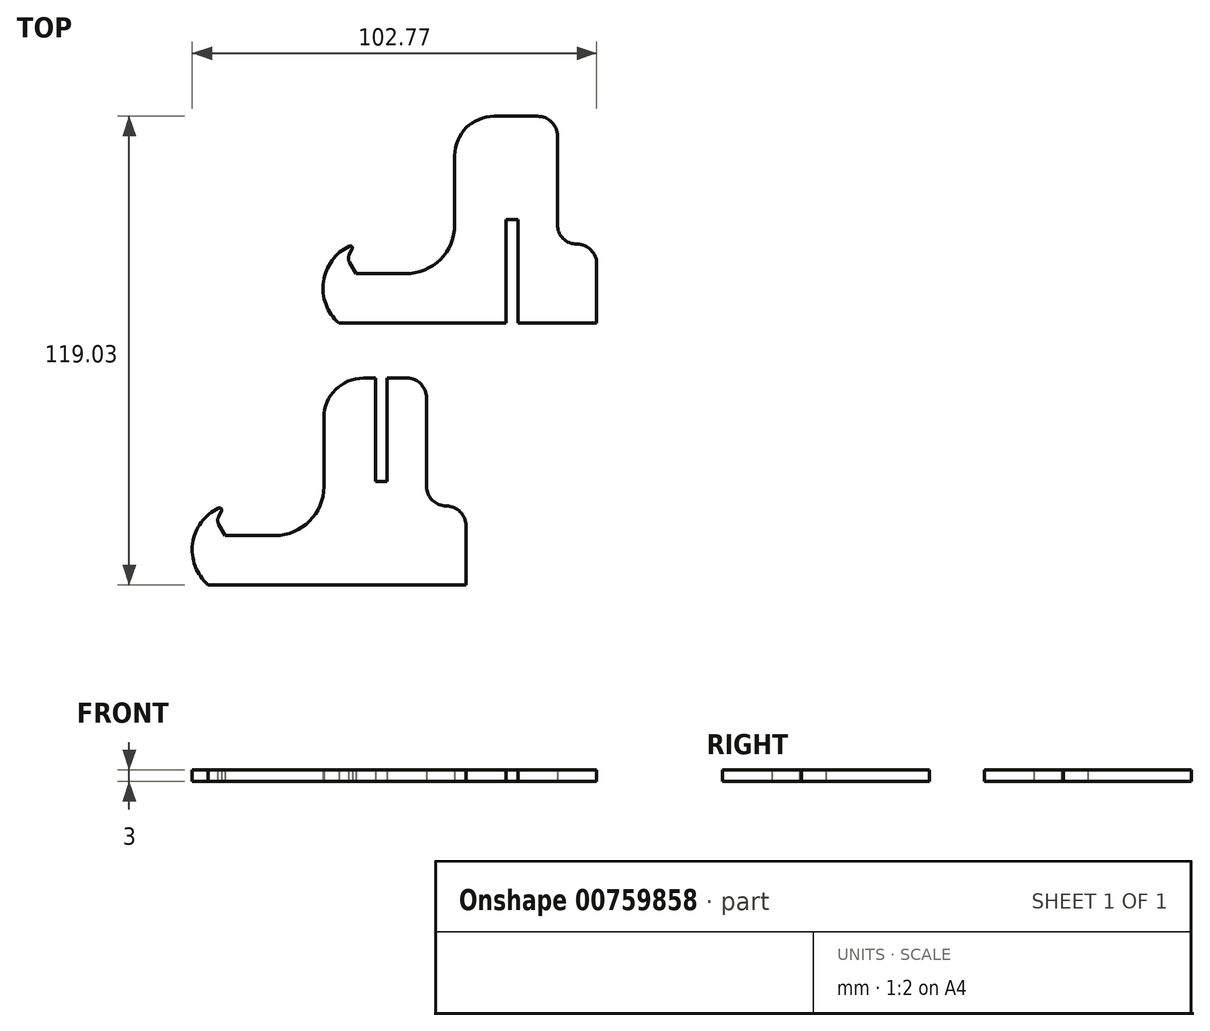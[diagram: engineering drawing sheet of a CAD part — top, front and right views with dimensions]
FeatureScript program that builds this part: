
annotation { "Feature Type Name" : "Feature", "Feature Type Description" : "" }
export const myFeature = defineFeature(function(context is Context, id is Id, definition is map)
    precondition{}
    {
        {
            var Q0;
            Q0=qCreatedBy(makeId("Top.planeOp"),FACE);
            var sketch = newSketch(context, id + "F0", { "sketchPlane" : qUnion([Q0])});
            skLineSegment(sketch, "E0", {"start": v(-16.1, 20.7) * mm, "end": v(-28.7, 20.7) * mm});
            skLineSegment(sketch, "E1", {"start": v(-28.7, 20.7) * mm, "end": v(-30.35, 23.55) * mm});
            skPoint(sketch, "E2.visualSharp", {"position": v(3.9, 50.7) * mm});
            skPoint(sketch, "E3.visualSharp", {"position": v(3.9, 20.7) * mm});
            skArc(sketch, "E3.filletArc", {"start": v(-16.1, 20.7) * mm, "mid": v(-7.26, 24.35) * mm, "end": v(-3.6, 33.2) * mm});
            skPoint(sketch, "E4.second.point", {"position": v(-37.03, 18.2) * mm});
            skPoint(sketch, "E5.orphan", {"position": v(-37.03, 28.2) * mm});
            skPoint(sketch, "E6.0.end.orphan", {"position": v(-37.03, 8.2) * mm});
            skLineSegment(sketch, "E7", {"start": v(-30.43, 25.38) * mm, "end": v(-29.67, 27.05) * mm});
            skArc(sketch, "E8", {"start": v(-30.34, 27.7) * mm, "mid": v(-36.97, 18.68) * mm, "end": v(-33.03, 8.2) * mm});
            skPoint(sketch, "E9.orphan", {"position": v(-33.03, 28.2) * mm});
            skPoint(sketch, "E10.visualSharp", {"position": v(-30.86, 24.44) * mm});
            skArc(sketch, "E10.filletArc", {"start": v(-30.43, 25.38) * mm, "mid": v(-30.61, 24.45) * mm, "end": v(-30.35, 23.55) * mm});
            skPoint(sketch, "E11.visualSharp", {"position": v(-29.14, 28.2) * mm});
            skArc(sketch, "E11.filletArc", {"start": v(-29.67, 27.05) * mm, "mid": v(-29.77, 27.61) * mm, "end": v(-30.34, 27.7) * mm});
            skLineSegment(sketch, "E12", {"start": v(-3.6, 33.2) * mm, "end": v(-3.6, 50.7) * mm});
            skPoint(sketch, "E13.visualSharp", {"position": v(-3.6, 60.7) * mm});
            skArc(sketch, "E13.filletArc", {"start": v(6.4, 60.7) * mm, "mid": v(-0.67, 57.76) * mm, "end": v(-3.6, 50.7) * mm});
            skLineSegment(sketch, "E14", {"start": v(-33.03, 8.2) * mm, "end": v(9.47, 8.2) * mm});
            skLineSegment(sketch, "E15", {"start": v(9.47, 8.2) * mm, "end": v(9.47, 34.44) * mm});
            skLineSegment(sketch, "E16", {"start": v(9.47, 34.44) * mm, "end": v(12.47, 34.44) * mm});
            skLineSegment(sketch, "E17", {"start": v(12.47, 34.44) * mm, "end": v(12.47, 8.2) * mm});
            skLineSegment(sketch, "E18", {"start": v(12.47, 8.2) * mm, "end": v(32.47, 8.2) * mm});
            skLineSegment(sketch, "E19", {"start": v(32.47, 8.2) * mm, "end": v(32.47, 23.2) * mm});
            skLineSegment(sketch, "E20", {"start": v(17.47, 60.7) * mm, "end": v(6.4, 60.7) * mm});
            skPoint(sketch, "E21.visualSharp", {"position": v(32.47, 60.7) * mm});
            skLineSegment(sketch, "E22", {"start": v(22.47, 33.2) * mm, "end": v(22.47, 55.7) * mm});
            skLineSegment(sketch, "E23", {"start": v(17.47, 60.7) * mm, "end": v(17.47, 60.7) * mm});
            skLineSegment(sketch, "E24.0", {"start": v(27.47, 28.2) * mm, "end": v(27.47, 28.2) * mm});
            skPoint(sketch, "E25.orphan", {"position": v(22.47, 8.2) * mm});
            skPoint(sketch, "E26.visualSharp", {"position": v(22.47, 60.7) * mm});
            skArc(sketch, "E26.filletArc", {"start": v(22.47, 55.7) * mm, "mid": v(21, 59.23) * mm, "end": v(17.47, 60.7) * mm});
            skPoint(sketch, "E27.visualSharp", {"position": v(22.47, 28.2) * mm});
            skArc(sketch, "E27.filletArc", {"start": v(22.47, 33.2) * mm, "mid": v(23.94, 29.66) * mm, "end": v(27.47, 28.2) * mm});
            skPoint(sketch, "E28.visualSharp", {"position": v(32.47, 28.2) * mm});
            skArc(sketch, "E28.filletArc", {"start": v(32.47, 23.2) * mm, "mid": v(31, 26.73) * mm, "end": v(27.47, 28.2) * mm});
            skLineSegment(sketch, "E29", {"start": v(-18.7, 20.7) * mm, "end": v(0.7, 62.1) * mm, "construction": true});
            skLineSegment(sketch, "E30", {"start": v(-49.32, -45.84) * mm, "end": v(-61.91, -45.84) * mm});
            skLineSegment(sketch, "E31", {"start": v(-61.91, -45.84) * mm, "end": v(-63.56, -42.99) * mm});
            skPoint(sketch, "E32.visualSharp", {"position": v(-29.32, -15.84) * mm});
            skPoint(sketch, "E33.visualSharp", {"position": v(-29.32, -45.84) * mm});
            skArc(sketch, "E33.filletArc", {"start": v(-49.32, -45.84) * mm, "mid": v(-40.48, -42.18) * mm, "end": v(-36.82, -33.34) * mm});
            skPoint(sketch, "E34.second.point", {"position": v(-70.24, -48.34) * mm});
            skPoint(sketch, "E35.orphan", {"position": v(-70.24, -38.34) * mm});
            skPoint(sketch, "E36.0.end.orphan", {"position": v(-70.24, -58.34) * mm});
            skLineSegment(sketch, "E37", {"start": v(-63.65, -41.15) * mm, "end": v(-62.88, -39.49) * mm});
            skArc(sketch, "E38", {"start": v(-63.55, -38.82) * mm, "mid": v(-70.19, -47.85) * mm, "end": v(-66.24, -58.34) * mm});
            skPoint(sketch, "E39.orphan", {"position": v(-66.24, -38.34) * mm});
            skPoint(sketch, "E40.visualSharp", {"position": v(-64.08, -42.1) * mm});
            skArc(sketch, "E40.filletArc", {"start": v(-63.65, -41.15) * mm, "mid": v(-63.83, -42.08) * mm, "end": v(-63.56, -42.99) * mm});
            skPoint(sketch, "E41.visualSharp", {"position": v(-62.36, -38.34) * mm});
            skArc(sketch, "E41.filletArc", {"start": v(-62.88, -39.49) * mm, "mid": v(-62.99, -38.92) * mm, "end": v(-63.55, -38.82) * mm});
            skLineSegment(sketch, "E42", {"start": v(-36.82, -33.34) * mm, "end": v(-36.82, -15.84) * mm});
            skPoint(sketch, "E43.visualSharp", {"position": v(-36.82, -5.84) * mm});
            skArc(sketch, "E43.filletArc", {"start": v(-26.82, -5.84) * mm, "mid": v(-33.89, -8.77) * mm, "end": v(-36.82, -15.84) * mm});
            skLineSegment(sketch, "E44", {"start": v(-66.24, -58.34) * mm, "end": v(-23.74, -58.34) * mm});
            skLineSegment(sketch, "E45", {"start": v(-23.74, -32.1) * mm, "end": v(-20.74, -32.1) * mm});
            skLineSegment(sketch, "E46", {"start": v(-20.74, -58.34) * mm, "end": v(-0.74, -58.34) * mm});
            skLineSegment(sketch, "E47", {"start": v(-0.74, -58.34) * mm, "end": v(-0.74, -43.34) * mm});
            skLineSegment(sketch, "E48", {"start": v(-15.74, -5.84) * mm, "end": v(-20.74, -5.84) * mm});
            skPoint(sketch, "E49.visualSharp", {"position": v(-0.74, -5.84) * mm});
            skLineSegment(sketch, "E50", {"start": v(-10.74, -33.34) * mm, "end": v(-10.74, -10.84) * mm});
            skLineSegment(sketch, "E51", {"start": v(-15.74, -5.84) * mm, "end": v(-15.74, -5.84) * mm});
            skLineSegment(sketch, "E52.0", {"start": v(-5.74, -38.34) * mm, "end": v(-5.74, -38.34) * mm});
            skPoint(sketch, "E53.orphan", {"position": v(-10.74, -58.34) * mm});
            skPoint(sketch, "E54.visualSharp", {"position": v(-10.74, -5.84) * mm});
            skArc(sketch, "E54.filletArc", {"start": v(-10.74, -10.84) * mm, "mid": v(-12.2, -7.3) * mm, "end": v(-15.74, -5.84) * mm});
            skPoint(sketch, "E55.visualSharp", {"position": v(-10.74, -38.34) * mm});
            skArc(sketch, "E55.filletArc", {"start": v(-10.74, -33.34) * mm, "mid": v(-9.28, -36.88) * mm, "end": v(-5.74, -38.34) * mm});
            skPoint(sketch, "E56.visualSharp", {"position": v(-0.74, -38.34) * mm});
            skArc(sketch, "E56.filletArc", {"start": v(-0.74, -43.34) * mm, "mid": v(-2.2, -39.8) * mm, "end": v(-5.74, -38.34) * mm});
            skLineSegment(sketch, "E57", {"start": v(-51.91, -45.84) * mm, "end": v(-32.52, -4.44) * mm, "construction": true});
            skLineSegment(sketch, "E58", {"start": v(-23.74, -32.1) * mm, "end": v(-23.74, -5.84) * mm});
            skLineSegment(sketch, "E59", {"start": v(-20.74, -32.1) * mm, "end": v(-20.74, -5.84) * mm});
            skLineSegment(sketch, "E60", {"start": v(-23.74, -58.34) * mm, "end": v(-20.74, -58.34) * mm});
            skLineSegment(sketch, "E61.trimOffspring", {"start": v(-23.74, -5.84) * mm, "end": v(-26.82, -5.84) * mm});
            skPoint(sketch, "E62.orphan", {"position": v(-56.24, -58.34) * mm});
            skPoint(sketch, "E63.orphan", {"position": v(-23.03, 8.2) * mm});
            skSolve(sketch);
        }
        {
            var Q0;
            Q0=makeQuery(id+"F0.imprint","IMPRINT",FACE,{"disambiguationData":[TD([[makeQuery(id+"F0.imprint","IMPRINT",EDGE,{"derivedFrom":sQuery(id+"F0.wireOp",EDGE,"E0")}),1.0]])]});
            var Q1;
            Q1=makeQuery(id+"F0.imprint","IMPRINT",FACE,{"disambiguationData":[TD([[makeQuery(id+"F0.imprint","IMPRINT",EDGE,{"derivedFrom":sQuery(id+"F0.wireOp",EDGE,"E30")}),1.0]])]});
            extrude(context, id + "F1", {"entities" : qUnion([Q0, Q1]), "depth" : 3 * mm});
        }
    });
